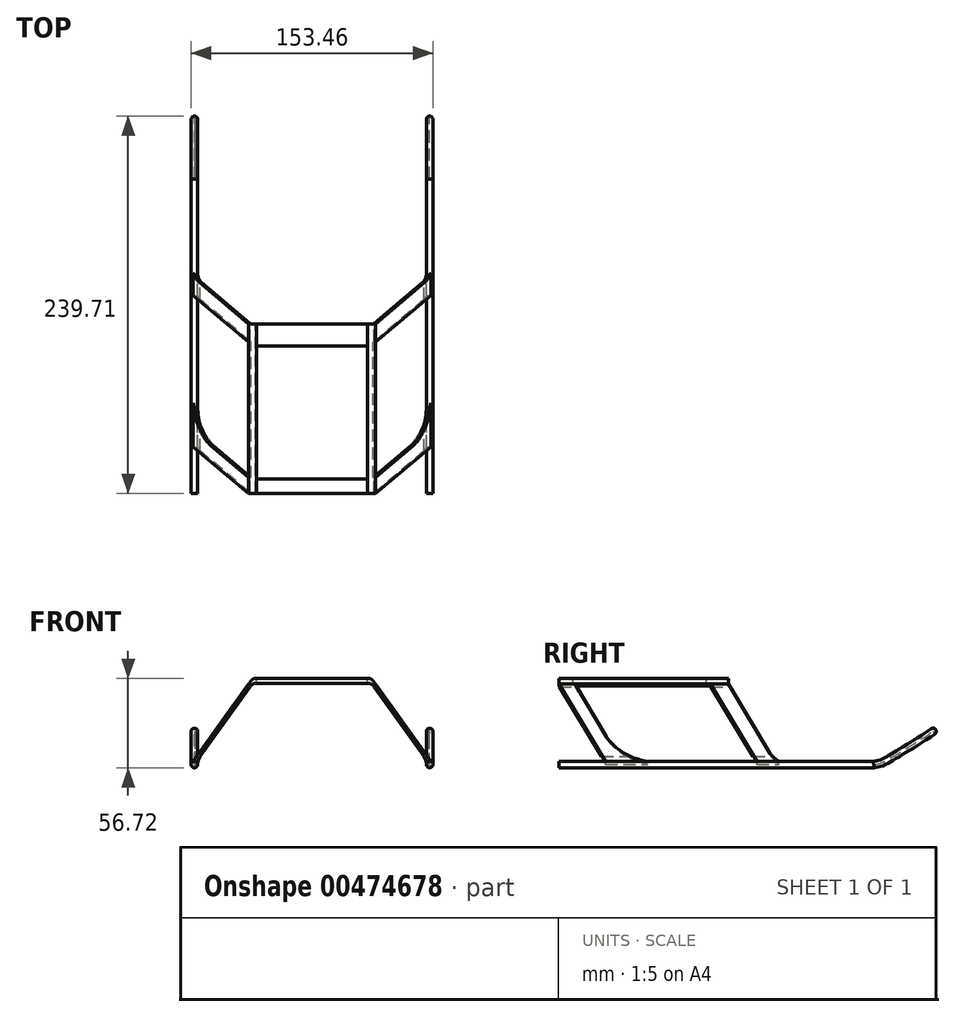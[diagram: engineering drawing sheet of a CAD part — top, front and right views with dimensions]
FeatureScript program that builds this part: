
annotation { "Feature Type Name" : "Feature", "Feature Type Description" : "" }
export const myFeature = defineFeature(function(context is Context, id is Id, definition is map)
    precondition{}
    {
        {
            var Q0;
            Q0=qCreatedBy(makeId("Front.planeOp"),FACE);
            var sketch = newSketch(context, id + "F0", { "sketchPlane" : qUnion([Q0])});
            skPoint(sketch, "E0.middle", {"position": v(0, 19.52) * mm});
            skLineSegment(sketch, "E1", {"start": v(0, 12.36) * mm, "end": v(0, 0) * mm});
            skCircle(sketch, "E2.MirrorC", {"center": v(74.68, -33.65) * mm, "radius": 2.05 * mm});
            skFitSpline(sketch, "E3.MirrorCS", {"points": [v(39.32, 15.73) * mm, v(37.7, 17.35) * mm, v(35.8, 18.02) * mm], "startDerivative": vector(-2.99, 3.8) * mm, "endDerivative": vector(-5.08, 0.78) * mm});
            skFitSpline(sketch, "E4.MirrorCS", {"points": [v(40.27, 17.42) * mm, v(37.7, 20.55) * mm, v(35.28, 21.02) * mm], "startDerivative": vector(-4.33, 6.82) * mm, "endDerivative": vector(-5.7, 0.11) * mm});
            skLineSegment(sketch, "E5.MirrorCS", {"start": v(39.32, 15.73) * mm, "end": v(73.48, -32) * mm});
            skLineSegment(sketch, "E6.MirrorCS", {"start": v(40.27, 17.42) * mm, "end": v(75.46, -31.76) * mm});
            skLineSegment(sketch, "E7", {"start": v(35.28, 21.02) * mm, "end": v(0, 21.02) * mm});
            skLineSegment(sketch, "E8", {"start": v(0, 21.02) * mm, "end": v(0, 18.02) * mm});
            skLineSegment(sketch, "E9", {"start": v(0, 18.02) * mm, "end": v(35.8, 18.02) * mm});
            skFitSpline(sketch, "E10", {"points": [v(71.05, -28.6) * mm, v(72.35, -31.43) * mm, v(72.64, -33.81) * mm], "startDerivative": vector(2.92, -5.35) * mm, "endDerivative": vector(0.19, -5.05) * mm});
            skSolve(sketch);
        }
        {
            var Q0;
            Q0 = qSketchRegion(id + "F0", true);
            extrude(context, id + "F1", {"entities" : qUnion([Q0]), "depth" : 140 * mm});
        }
        {
            var Q0;
            Q0=makeQuery(id+"F1.opExtrude","CAP_FACE",FACE,{"disambiguationData":[OSD([sQuery(id+"F0.wireOp",EDGE,"54897e89-243a-4544-b714-c302b4b4ef84"),sQuery(id+"F0.wireOp",EDGE,"E2.MirrorC"),sQuery(id+"F0.wireOp",EDGE,"570e788b-86fd-4a2f-8e09-bb03b35ab2ee"),sQuery(id+"F0.wireOp",EDGE,"9363e714-197f-42d5-b9f4-1de75f6270ba"),sQuery(id+"F0.wireOp",EDGE,"E3.MirrorCS"),sQuery(id+"F0.wireOp",EDGE,"E4.MirrorCS"),sQuery(id+"F0.wireOp",EDGE,"jA9nAWp6-H2hY-529Y-rH8D-cFilVRpV2U5K"),sQuery(id+"F0.wireOp",EDGE,"S6O7i2Qb-M4bX-xLsD-Uy3w-F3S5Ko65z9Zw"),sQuery(id+"F0.wireOp",EDGE,"75VxtiKv-752z-kq7p-fFpC-obT0bSKGjdlB"),sQuery(id+"F0.wireOp",EDGE,"wJ8BZcal-cRkY-BvQC-AXGJ-Mzpq5TT2z513"),sQuery(id+"F0.wireOp",EDGE,"E5.MirrorCS"),sQuery(id+"F0.wireOp",EDGE,"E6.MirrorCS")])],"isStart":true});
            var sketch = newSketch(context, id + "F2", { "sketchPlane" : qUnion([Q0])});
            skCircle(sketch, "E11", {"center": v(-74.68, -33.65) * mm, "radius": 2.05 * mm});
            skCircle(sketch, "E12", {"center": v(74.68, -33.65) * mm, "radius": 2.05 * mm});
            skSolve(sketch);
        }
        {
            var Q0;
            Q0=makeQuery(id+"F1.opExtrude","SWEPT_FACE",FACE,{"disambiguationData":[OSD([sQuery(id+"F0.wireOp",EDGE,"E6.MirrorCS")])]});
            var sketch = newSketch(context, id + "F3", { "sketchPlane" : qUnion([Q0])});
            skLineSegment(sketch, "E13", {"start": v(-120.87, -9.27) * mm, "end": v(-43.79, -9.27) * mm});
            skLineSegment(sketch, "E14", {"start": v(-43.79, -9.27) * mm, "end": v(-14.1, -69.74) * mm});
            skLineSegment(sketch, "E15", {"start": v(-14.1, -69.74) * mm, "end": v(-100.2, -69.74) * mm});
            skLineSegment(sketch, "E16", {"start": v(-100.2, -69.74) * mm, "end": v(-129.88, -9.27) * mm});
            skLineSegment(sketch, "E17", {"start": v(-129.88, -9.27) * mm, "end": v(-120.87, -9.27) * mm});
            skLineSegment(sketch, "E18", {"start": v(-140, -9.27) * mm, "end": v(-110.32, -69.74) * mm});
            skLineSegment(sketch, "E19", {"start": v(-110.32, -69.74) * mm, "end": v(-140, -69.74) * mm});
            skLineSegment(sketch, "E20", {"start": v(-140, -69.74) * mm, "end": v(-140, -9.27) * mm});
            skLineSegment(sketch, "E21", {"start": v(-32.36, -9.27) * mm, "end": v(-2.68, -69.74) * mm});
            skLineSegment(sketch, "E22", {"start": v(-2.68, -69.74) * mm, "end": v(0, -69.74) * mm});
            skLineSegment(sketch, "E23", {"start": v(0, -69.74) * mm, "end": v(0, -9.27) * mm});
            skLineSegment(sketch, "E24", {"start": v(0, -9.27) * mm, "end": v(-32.36, -9.27) * mm});
            skArc(sketch, "E25", {"start": v(-109.57, -50.65) * mm, "mid": v(-98.31, -63.31) * mm, "end": v(-82.63, -69.74) * mm});
            skArc(sketch, "E26", {"start": v(-5.76, -63.46) * mm, "mid": v(-3.17, -66.87) * mm, "end": v(0, -69.74) * mm});
            skSolve(sketch);
        }
        {
            var Q0;
            Q0=makeQuery(id+"F3.imprint","IMPRINT",FACE,{"disambiguationData":[TD([[makeQuery(id+"F3.imprint","IMPRINT",EDGE,{"derivedFrom":sQuery(id+"F3.wireOp",EDGE,"E13")}),-1.0]])]});
            var Q1;
            Q1=makeQuery(id+"F3.imprint","IMPRINT",FACE,{"disambiguationData":[TD([[makeQuery(id+"F3.imprint","IMPRINT",EDGE,{"derivedFrom":sQuery(id+"F3.wireOp",EDGE,"E18")}),-1.0]])]});
            var Q2;
            Q2=makeQuery(id+"F3.imprint","IMPRINT",FACE,{"disambiguationData":[TD([[makeQuery(id+"F3.imprint","IMPRINT",EDGE,{"derivedFrom":sQuery(id+"F3.wireOp",EDGE,"E23")}),-1.0]])]});
            extrude(context, id + "F4", {"entities" : qUnion([Q0, Q1, Q2]), "operationType" : NewBodyOperationType.REMOVE, "oppositeDirection" : true, "depth" : 5 * mm});
        }
        {
            var Q0;
            {var subQ0=sQuery(id+"F2.wireOp",EDGE,"E11");var subQ1=makeQuery(id+"F2.imprint","INTERSECT",VERTEX,{"derivedFrom":[makeQuery(id+"F1.opExtrude","CAP_EDGE",EDGE,{"disambiguationData":[OSD([sQuery(id+"F0.wireOp",EDGE,"E5.MirrorCS")])],"isStart":true}),subQ0]});Q0=makeQuery(id+"F2.imprint","IMPRINT",FACE,{"disambiguationData":[TD([[makeQuery(id+"F2.imprint","IMPRINT",EDGE,{"disambiguationData":[TD([[subQ1,-1.0]])],"derivedFrom":subQ0}),1.0]])]});}
            extrude(context, id + "F5", {"entities" : qUnion([Q0]), "operationType" : NewBodyOperationType.ADD, "depth" : 35 * mm});
        }
        {
            var Q0;
            {var subQ0=sQuery(id+"F0.wireOp",EDGE,"E2.MirrorC");Q0=makeQuery(id+"F4.boolean.opBoolean","SPLIT",FACE,{"disambiguationData":[TD([makeQuery(id+"F1.opExtrude","SWEPT_FACE",FACE,{"disambiguationData":[OSD([subQ0])]})])],"derivedFrom":makeQuery(id+"F1.opExtrude","CAP_FACE",FACE,{"disambiguationData":[OSD([subQ0,sQuery(id+"F0.wireOp",EDGE,"E3.MirrorCS"),sQuery(id+"F0.wireOp",EDGE,"E4.MirrorCS"),sQuery(id+"F0.wireOp",EDGE,"E5.MirrorCS"),sQuery(id+"F0.wireOp",EDGE,"E6.MirrorCS"),sQuery(id+"F0.wireOp",EDGE,"E7"),sQuery(id+"F0.wireOp",EDGE,"E8"),sQuery(id+"F0.wireOp",EDGE,"E9")])],"isStart":false})});}
            var sketch = newSketch(context, id + "F6", { "sketchPlane" : qUnion([Q0])});
            skCircle(sketch, "E27", {"center": v(74.68, -33.65) * mm, "radius": 2.05 * mm});
            skSolve(sketch);
        }
        {
            var Q0;
            Q0=makeQuery(id+"F6.imprint","IMPRINT",FACE,{"disambiguationData":[TD([[makeQuery(id+"F6.imprint","IMPRINT",EDGE,{"disambiguationData":[OD(0.0)],"derivedFrom":sQuery(id+"F6.wireOp",EDGE,"E27")}),1.0]])]});
            var Q1;
            Q1=makeQuery(id+"F6.imprint","IMPRINT",FACE,{"disambiguationData":[TD([[makeQuery(id+"F6.imprint","IMPRINT",EDGE,{"disambiguationData":[OD(1.0)],"derivedFrom":sQuery(id+"F6.wireOp",EDGE,"E27")}),-1.0]])]});
            extrude(context, id + "F7", {"entities" : qUnion([Q0, Q1]), "operationType" : NewBodyOperationType.ADD, "oppositeDirection" : true, "depth" : 150 * mm});
        }
        {
            var Q0;
            Q0=makeQuery(id+"F1.opExtrude","SWEPT_FACE",FACE,{"disambiguationData":[OSD([sQuery(id+"F0.wireOp",EDGE,"E7")])]});
            var sketch = newSketch(context, id + "F8", { "sketchPlane" : qUnion([Q0])});
            skLineSegment(sketch, "E28.bottom", {"start": v(0, -130.93) * mm, "end": v(35.28, -130.93) * mm});
            skLineSegment(sketch, "E28.top", {"start": v(0, -46.27) * mm, "end": v(35.28, -46.27) * mm});
            skLineSegment(sketch, "E28.left", {"start": v(0, -130.93) * mm, "end": v(0, -46.27) * mm});
            skLineSegment(sketch, "E28.right", {"start": v(35.28, -130.93) * mm, "end": v(35.28, -46.27) * mm});
            skLineSegment(sketch, "E29.bottom", {"start": v(0, -32.3) * mm, "end": v(35.28, -32.3) * mm});
            skLineSegment(sketch, "E29.top", {"start": v(0, 0) * mm, "end": v(35.28, 0) * mm});
            skLineSegment(sketch, "E29.left", {"start": v(0, -32.3) * mm, "end": v(0, 0) * mm});
            skLineSegment(sketch, "E29.right", {"start": v(35.28, -32.3) * mm, "end": v(35.28, 0) * mm});
            skSolve(sketch);
        }
        {
            var Q0;
            Q0=makeQuery(id+"F8.imprint","IMPRINT",FACE,{"disambiguationData":[TD([[makeQuery(id+"F8.imprint","IMPRINT",EDGE,{"derivedFrom":sQuery(id+"F8.wireOp",EDGE,"E28.bottom")}),1.0]])]});
            var Q1;
            Q1=makeQuery(id+"F8.imprint","IMPRINT",FACE,{"disambiguationData":[TD([[makeQuery(id+"F8.imprint","IMPRINT",EDGE,{"derivedFrom":sQuery(id+"F8.wireOp",EDGE,"E29.bottom")}),1.0]])]});
            extrude(context, id + "F9", {"entities" : qUnion([Q0, Q1]), "operationType" : NewBodyOperationType.REMOVE, "oppositeDirection" : true, "depth" : 5 * mm});
        }
        {
            var Q0;
            {var subQ0=sQuery(id+"F0.wireOp",EDGE,"E7");var subQ1=sQuery(id+"F0.wireOp",EDGE,"E4.MirrorCS");var subQ2=sQuery(id+"F0.wireOp",EDGE,"E8");var subQ3=sQuery(id+"F0.wireOp",EDGE,"E3.MirrorCS");var subQ4=sQuery(id+"F0.wireOp",EDGE,"E9");Q0=makeQuery(id+"F4.boolean.opBoolean","SPLIT",FACE,{"disambiguationData":[TD([makeQuery(id+"F1.opExtrude","SWEPT_FACE",FACE,{"disambiguationData":[OSD([subQ3])]})])],"derivedFrom":makeQuery(id+"F1.opExtrude","CAP_FACE",FACE,{"disambiguationData":[OSD([sQuery(id+"F0.wireOp",EDGE,"E2.MirrorC"),subQ3,subQ1,sQuery(id+"F0.wireOp",EDGE,"E5.MirrorCS"),sQuery(id+"F0.wireOp",EDGE,"E6.MirrorCS"),subQ0,subQ2,subQ4])],"isStart":true})});}
            extrude(context, id + "F10", {"entities" : qUnion([Q0]), "operationType" : NewBodyOperationType.REMOVE, "oppositeDirection" : true, "depth" : 32.3 * mm});
        }
        {
            var Q0;
            Q0=makeQuery(id+"F5.opExtrude","CAP_FACE",FACE,{"disambiguationData":[OSD([sQuery(id+"F2.wireOp",EDGE,"E11")])],"isStart":false});
            var sketch = newSketch(context, id + "F11", { "sketchPlane" : qUnion([Q0])});
            skLineSegment(sketch, "E30.bottom", {"start": v(-74.68, -33.65) * mm, "end": v(-74.02, -33.65) * mm});
            skLineSegment(sketch, "E30.top", {"start": v(-74.68, -35.09) * mm, "end": v(-74.02, -35.09) * mm});
            skLineSegment(sketch, "E30.left", {"start": v(-74.68, -33.65) * mm, "end": v(-74.68, -35.09) * mm});
            skLineSegment(sketch, "E30.right", {"start": v(-74.02, -33.65) * mm, "end": v(-74.02, -35.09) * mm});
            skSolve(sketch);
        }
        {
            var Q0;
            Q0=makeQuery(id+"F11.imprint","IMPRINT",FACE,{"disambiguationData":[TD([[makeQuery(id+"F11.imprint","IMPRINT",EDGE,{"derivedFrom":sQuery(id+"F11.wireOp",EDGE,"E30.bottom")}),-1.0]])]});
            extrude(context, id + "F12", {"entities" : qUnion([Q0]), "operationType" : NewBodyOperationType.ADD, "depth" : 25 * mm});
        }
        {
            var Q0;
            Q0=makeQuery(id+"F12.opExtrude","SWEPT_FACE",FACE,{"disambiguationData":[OSD([sQuery(id+"F11.wireOp",EDGE,"E30.left")])]});
            var sketch = newSketch(context, id + "F13", { "sketchPlane" : qUnion([Q0])});
            skLineSegment(sketch, "E31", {"start": v(35, -33.65) * mm, "end": v(60, -33.65) * mm});
            skLineSegment(sketch, "E32", {"start": v(60, -33.65) * mm, "end": v(60, -35.7) * mm});
            skLineSegment(sketch, "E33", {"start": v(60, -35.7) * mm, "end": v(35, -35.7) * mm});
            skLineSegment(sketch, "E34", {"start": v(35, -35.7) * mm, "end": v(35, -33.65) * mm});
            skFitSpline(sketch, "E35", {"points": [v(60, -33.65) * mm, v(64.8, -32.6) * mm, v(71.7, -28.95) * mm, v(85.9, -20.33) * mm, v(95.44, -14.17) * mm, v(97.66, -12.58) * mm], "startDerivative": vector(30.33, 4.53) * mm, "endDerivative": vector(15.8, 11.66) * mm});
            skFitSpline(sketch, "E36.0", {"points": [v(60.3, -35.68) * mm, v(60.93, -35.59) * mm, v(61.92, -35.44) * mm, v(63.3, -35.17) * mm, v(64.18, -34.95) * mm, v(64.9, -34.73) * mm, v(65.46, -34.55) * mm, v(66, -34.34) * mm, v(66.74, -34.04) * mm, v(67.65, -33.62) * mm, v(69.11, -32.86) * mm, v(70.63, -31.98) * mm, v(72.27, -31) * mm, v(74.02, -29.94) * mm, v(76.44, -28.5) * mm, v(79.57, -26.6) * mm, v(82.8, -24.64) * mm, v(86.04, -22.66) * mm, v(89.15, -20.71) * mm, v(92, -18.9) * mm, v(94.08, -17.55) * mm, v(95.5, -16.61) * mm, v(96.42, -15.99) * mm, v(97.19, -15.46) * mm, v(98.04, -14.85) * mm, v(98.55, -14.48) * mm, v(98.88, -14.23) * mm]});
            skLineSegment(sketch, "E37", {"start": v(60, -35.7) * mm, "end": v(60.3, -35.68) * mm});
            skLineSegment(sketch, "E38", {"start": v(97.66, -12.58) * mm, "end": v(98.88, -14.23) * mm});
            skSolve(sketch);
        }
        {
            var Q0;
            Q0=makeQuery(id+"F5.opExtrude","CAP_FACE",FACE,{"disambiguationData":[OSD([sQuery(id+"F2.wireOp",EDGE,"E11")])],"isStart":false});
            var Q1;
            Q1=sQuery(id+"F13.wireOp",EDGE,"E31");
            var Q2;
            Q2=sQuery(id+"F13.wireOp",EDGE,"E35");
            sweep(context, id + "F14", {"operationType" : NewBodyOperationType.ADD, "profiles" : qUnion([Q0]), "path" : qUnion([Q1, Q2])});
        }
        {
            var Q0;
            Q0=makeQuery(id+"F14.opSweep","SWEPT_FACE",FACE,{"disambiguationData":[OSD([sQuery(id+"F11.wireOp",EDGE,"E30.left"),sQuery(id+"F13.wireOp",EDGE,"E31")])]});
            var sketch = newSketch(context, id + "F15", { "sketchPlane" : qUnion([Q0])});
            skCircle(sketch, "E39", {"center": v(-97.66, -12.58) * mm, "radius": 2.05 * mm});
            skLineSegment(sketch, "E40", {"start": v(-97.66, -12.58) * mm, "end": v(-98.88, -14.23) * mm});
            skLineSegment(sketch, "E41", {"start": v(-97.66, -12.58) * mm, "end": v(-96.45, -10.93) * mm});
            skLineSegment(sketch, "E42", {"start": v(-97.66, -12.58) * mm, "end": v(-97.04, -13.04) * mm});
            skLineSegment(sketch, "E43", {"start": v(-97.66, -12.58) * mm, "end": v(-99.31, -11.37) * mm});
            skSolve(sketch);
        }
        {
            var Q0;
            {var subQ3=sQuery(id+"F15.wireOp",EDGE,"E41");Q0=makeQuery(id+"F15.imprint","IMPRINT",FACE,{"disambiguationData":[TD([[makeQuery(id+"F15.imprint","IMPRINT",EDGE,{"derivedFrom":subQ3}),1.0]])]});}
            var Q1;
            Q1=sQuery(id+"F15.wireOp",EDGE,"E43");
            revolve(context, id + "F16", {"entities" : qUnion([Q0]), "axis" : qUnion([Q1]), "revolveType" : RevolveType.FULL});
        }
        {
            var Q0;
            Q0=makeQuery(id+"F1.opExtrude","SWEPT_BODY",BODY,{"disambiguationData":[OSD([sQuery(id+"F0.wireOp",EDGE,"E2.MirrorC"),sQuery(id+"F0.wireOp",EDGE,"E3.MirrorCS"),sQuery(id+"F0.wireOp",EDGE,"E4.MirrorCS"),sQuery(id+"F0.wireOp",EDGE,"E5.MirrorCS"),sQuery(id+"F0.wireOp",EDGE,"E6.MirrorCS"),sQuery(id+"F0.wireOp",EDGE,"E7"),sQuery(id+"F0.wireOp",EDGE,"E8"),sQuery(id+"F0.wireOp",EDGE,"E9"),sQuery(id+"F0.wireOp",EDGE,"E10")])]});
            var Q1;
            Q1=makeQuery(id+"F16.opRevolve","SWEPT_BODY",BODY,{"disambiguationData":[OSD([sQuery(id+"F15.wireOp",EDGE,"E39"),sQuery(id+"F15.wireOp",EDGE,"E41"),sQuery(id+"F15.wireOp",EDGE,"E43")])]});
            var Q2;
            Q2=qCreatedBy(makeId("Right.planeOp"),FACE);
            mirror(context, id + "F17", {"operationType" : NewBodyOperationType.ADD, "entities" : qUnion([Q0, Q1]), "mirrorPlane" : qUnion([Q2])});
        }
    });
